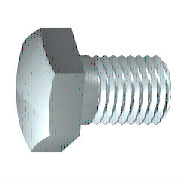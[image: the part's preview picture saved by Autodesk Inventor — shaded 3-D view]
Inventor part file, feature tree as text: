
AUTODESK INVENTOR PART (.ipt)
format: ipt  version: 2023.1 (Build 271208000, 208)  size: 190,976 bytes
history: native  units: mm (DEFAULTED — no unit token found)
features: sketch x3, extrude x1, chamfer x1, plane x1
ambient origin geometry x7: Origin, YZ Plane, XZ Plane, X Axis, Y Axis, Z Axis, Center Point
bodies: Solid1 (feature_tree), Body (feature_tree)
feature tree (6):
  extrude  "Head"  Depth=114.0mm
  chamfer  "Chamfer1"  Distance=9.2mm
  plane  "Work Plane1"
  sketch  "Sketch1"  dims[d0=120.0mm d1=114.0mm]
  sketch  "Sketch2"  dims[d2=16.0mm]
  sketch  "Sketch4"  dims[d12=90.0deg d3=9.2mm d4=0.0mm d5=30.0deg d21=90.0deg d6=1.2269mm d7=1.227mm d8=0.0mm d9=0.8001mm d10=22.49mm d11=24.0mm d13=1.227mm d14=16.0mm d15=114.0mm d16=0.0mm d19=24.0mm d55=45.0deg d57=0.0mm d58=0.0mm]
